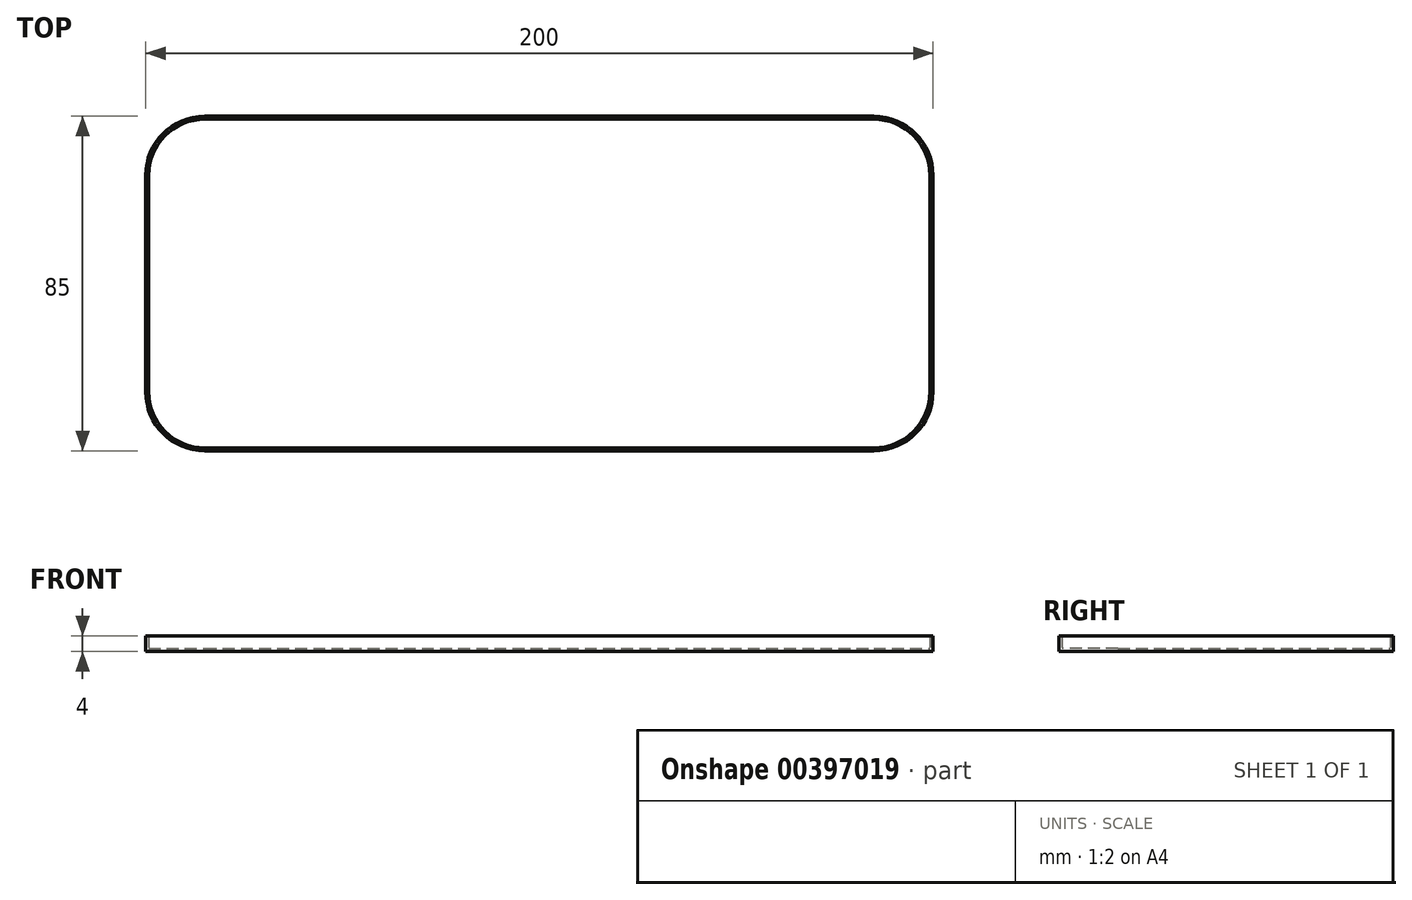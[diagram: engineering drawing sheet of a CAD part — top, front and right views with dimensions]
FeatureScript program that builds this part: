
annotation { "Feature Type Name" : "Feature", "Feature Type Description" : "" }
export const myFeature = defineFeature(function(context is Context, id is Id, definition is map)
    precondition{}
    {
        {
            var Q0;
            Q0=qCreatedBy(makeId("Top.planeOp"),FACE);
            var sketch = newSketch(context, id + "F0", { "sketchPlane" : qUnion([Q0])});
            skLineSegment(sketch, "E0.bottom", {"start": v(0, 0) * mm, "end": v(200, 0) * mm});
            skLineSegment(sketch, "E0.top", {"start": v(0, 85) * mm, "end": v(200, 85) * mm});
            skLineSegment(sketch, "E0.left", {"start": v(0, 0) * mm, "end": v(0, 85) * mm});
            skLineSegment(sketch, "E0.right", {"start": v(200, 0) * mm, "end": v(200, 85) * mm});
            skSolve(sketch);
        }
        {
            var Q0;
            Q0 = qSketchRegion(id + "F0", true);
            extrude(context, id + "F1", {"entities" : qUnion([Q0]), "oppositeDirection" : true, "depth" : 4 * mm});
        }
        {
            var Q0;
            Q0=makeQuery(id+"F1.opExtrude","SWEPT_EDGE",EDGE,{"disambiguationData":[OSD([sQuery(id+"F0.wireOp",EDGE,"E0.bottom"),sQuery(id+"F0.wireOp",EDGE,"E0.left")])]});
            var Q1;
            Q1=makeQuery(id+"F1.opExtrude","SWEPT_EDGE",EDGE,{"disambiguationData":[OSD([sQuery(id+"F0.wireOp",EDGE,"E0.bottom"),sQuery(id+"F0.wireOp",EDGE,"E0.right")])]});
            var Q2;
            Q2=makeQuery(id+"F1.opExtrude","SWEPT_EDGE",EDGE,{"disambiguationData":[OSD([sQuery(id+"F0.wireOp",EDGE,"E0.top"),sQuery(id+"F0.wireOp",EDGE,"E0.right")])]});
            var Q3;
            Q3=makeQuery(id+"F1.opExtrude","SWEPT_EDGE",EDGE,{"disambiguationData":[OSD([sQuery(id+"F0.wireOp",EDGE,"E0.top"),sQuery(id+"F0.wireOp",EDGE,"E0.left")])]});
            fillet(context, id + "F2", {"entities" : qUnion([Q0, Q1, Q2, Q3]), "radius" : 15 * mm, "tangentPropagation" : true, "allowEdgeOverflow" : false});
        }
        {
            var Q0;
            Q0=makeQuery(id+"F1.opExtrude","CAP_FACE",FACE,{"disambiguationData":[OSD([sQuery(id+"F0.wireOp",EDGE,"E0.bottom"),sQuery(id+"F0.wireOp",EDGE,"E0.top"),sQuery(id+"F0.wireOp",EDGE,"E0.left"),sQuery(id+"F0.wireOp",EDGE,"E0.right")])],"isStart":true});
            shell(context, id + "F3", {"entities" : qUnion([Q0]), "thickness" : .75 * mm});
        }
    });
